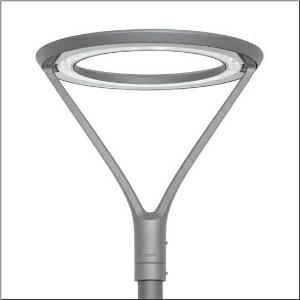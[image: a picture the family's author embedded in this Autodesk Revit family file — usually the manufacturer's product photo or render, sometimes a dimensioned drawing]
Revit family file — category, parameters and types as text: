
# Revit family: dl_20___p1_0a_5xa512836r008p_cf17
name_source: partatom
category: Lighting Fixtures
units: mm (PartAtom-declared; Revit-internal decimal feet)

## family parameters
Cut with Voids When Loaded = No
Host = Face
Light Source = No
Part Type = Normal
Room Calculation Point = No
Round Connector Dimension = Use Diameter
Shared = No

## types (1)
- --- (1 x LED, 4220 lm, 40.6 W, 2700K)
    Apparent Load = 41 VA
    CIE Flux Codes = 31 71 96 100 100
    Color Rendering = 70
    Color Temperature = 2700K
    Default Elevation = 1800 mm
    Description = DL® 20, mast luminaire, primary light control with cycle path optic, highly specular, primary optical cover: cover, of toughened safety glass of clear glass with excellent transmission level, light distribution: P1.0a, light emission: direct distribution, primary light characteristic: asymmetric, installation type: post-top, LED, High Power LED, rated luminous flux: 4.220lm, luminous efficacy: 104lm/W, light colour: 727, colour temperature: 2700K, control gear: Plus, control: flexible luminous flux parameterisation, time-dependent luminous flux control, constant luminous flux control, digital communication interface, power reduction, overheat protection, electronic power reduction, mains connection: 220..240V, 50/60Hz, connection cable pre-assembled, cable length: 5m, start of lifetime: 41W, end of service life: 42W, reduction: 20W, luminaire housing, upper part, of cast aluminium, powder-coated, Siteco® metallic grey (DB 702S), diameter: 690mm, height: 690mm, spigot size: 76mm (post-top), mounting height: 4..6m, luminaire housing, of cast aluminium, powder-coated, Siteco® metallic grey (DB 702S), equipment: Power, protection rating (complete): IP66, insulation class (complete): insulation class II (safety insulation), certification: CE, ENEC, VDE, impact resistance: IK08, permissible operating ambient temperature: -25..+30°C, standard-compliant lighting for roads and squares, packaging unit: 1 piece

Light Distribution: P1.0a
    Height = 690 mm
    Lamp = 1 x LED
    Lamp Light Flux = 4220 lm
    Lamp Power = 40.6 W
    Lamp count = 1
    Length = 690 mm
    Luminous efficacy = 104 lm/W
    Manufacturer = Siteco
    ModVariant = No
    Model = 5XA512836R008P
    Number of Poles = 1
    OnlyDefault = Yes
    Power Factor = 1
    Product Name = DL 20 | P1.0a
    Product group = mast luminaire | pylon top
    ProductGroupID = 6100
    Protection Class = Protection class II
    Protection Degree = IP 66
    RLX_Detail_Level = 1
    RLX_Emergency_Light_Flux = 0 lm
    RLX_Emergency_Type = 0
    RLX_Emergency_Type_DB = No
    RlxData = <blob elided: 206853 chars, md5=5971c0d0>
    Socket = socket
    Standby Power = 0 W
    System Light Flux = 4220 lm
    System Power = 41 W
    Type Comments = factory setting: luminous flux: 100 % | dim-lin: 254 | 549 mA
    Type Image = l_1006001.jpg
    URL = http://relux.com
    VarID = @adj_084783
    Voltage = 0 V
    Weight = 0.00 kg
    Width = 0 mm  [stored 0 ft]

note: [stored X ft] marks values corroborated as IEEE doubles in the binary element streams (Revit-internal decimal feet)

## geometry (parser evidence)
native form markers: Blend x4, Sweep x11
no freeform markers — native parametric forms only
